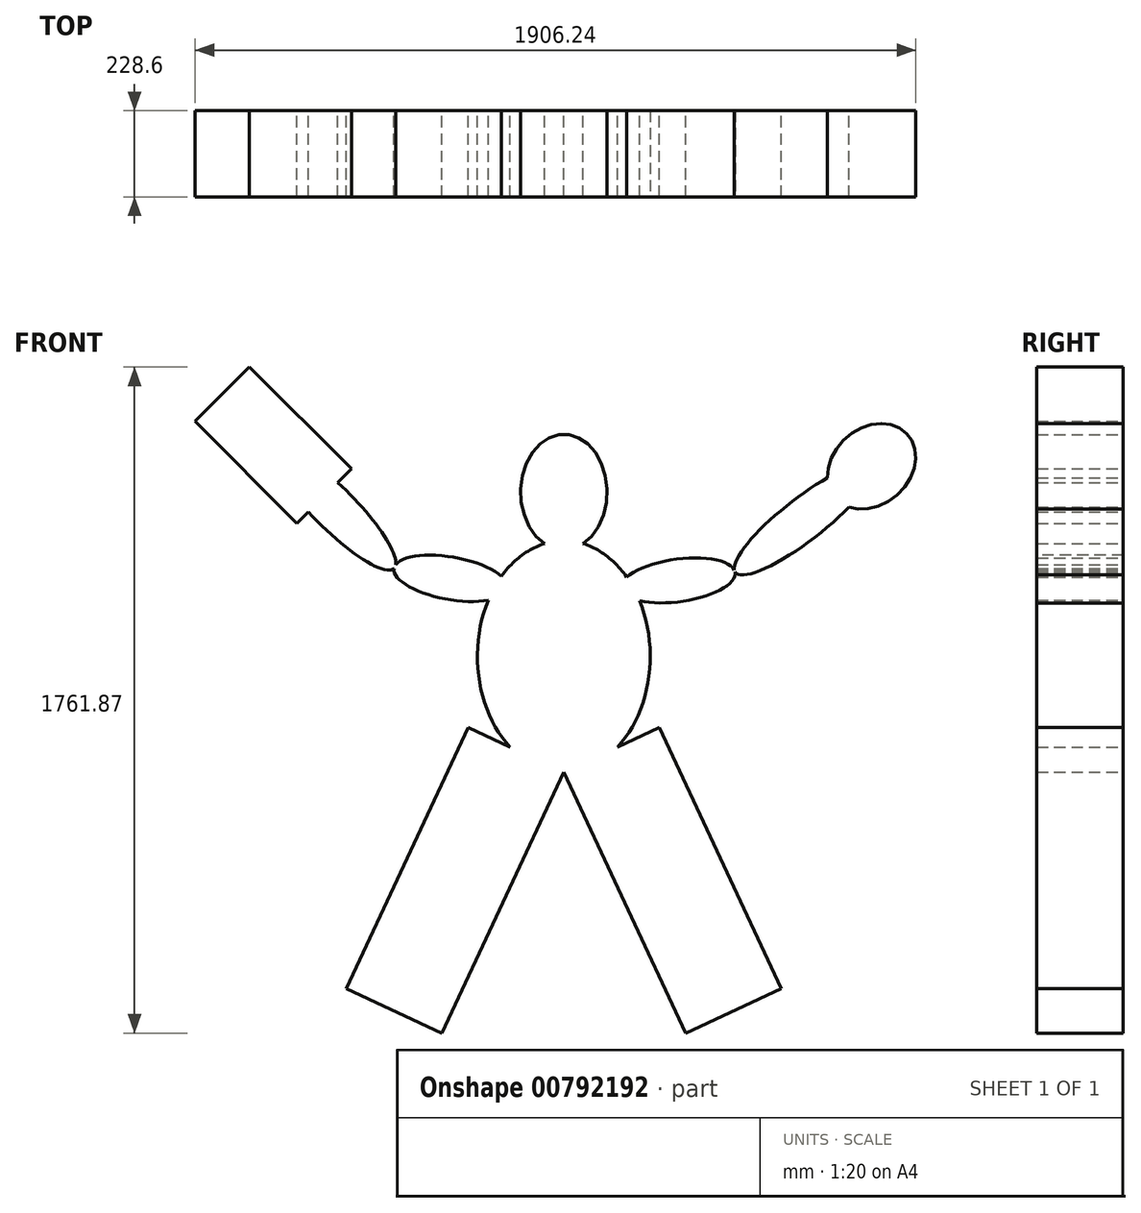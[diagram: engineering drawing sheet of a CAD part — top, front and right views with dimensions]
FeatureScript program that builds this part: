
annotation { "Feature Type Name" : "Feature", "Feature Type Description" : "" }
export const myFeature = defineFeature(function(context is Context, id is Id, definition is map)
    precondition{}
    {
        {
            var Q0;
            Q0=qCreatedBy(makeId("Front.planeOp"),FACE);
            var sketch = newSketch(context, id + "F0", { "sketchPlane" : qUnion([Q0])});
            skLineSegment(sketch, "E0.bottom", {"start": v(-670.73, 790.09) * mm, "end": v(-417.5, 908.17) * mm});
            skLineSegment(sketch, "E0.top", {"start": v(-348.7, 99.48) * mm, "end": v(-95.47, 217.56) * mm});
            skLineSegment(sketch, "E0.left", {"start": v(-670.73, 790.09) * mm, "end": v(-348.7, 99.48) * mm});
            skLineSegment(sketch, "E0.right", {"start": v(-417.5, 908.17) * mm, "end": v(-95.47, 217.56) * mm});
            skLineSegment(sketch, "E1", {"start": v(-670.73, 790.09) * mm, "end": v(-670.73, 666.94) * mm, "construction": true});
            skLineSegment(sketch, "E2.MirrorCS", {"start": v(-670.73, 790.09) * mm, "end": v(-992.76, 99.48) * mm});
            skLineSegment(sketch, "E3.MirrorCS", {"start": v(-670.73, 790.09) * mm, "end": v(-923.95, 908.17) * mm});
            skLineSegment(sketch, "E4.MirrorCS", {"start": v(-923.95, 908.17) * mm, "end": v(-1245.99, 217.56) * mm});
            skLineSegment(sketch, "E5.MirrorCS", {"start": v(-992.76, 99.48) * mm, "end": v(-1245.99, 217.56) * mm});
            skSolve(sketch);
        }
        {
            var Q0;
            Q0 = qSketchRegion(id + "F0", true);
            extrude(context, id + "F1", {"entities" : qUnion([Q0]), "depth" : 228.6 * mm, "offsetDistance" : 30.48 * mm});
        }
        {
            var Q0;
            Q0=qCreatedBy(makeId("Front.planeOp"),FACE);
            var sketch = newSketch(context, id + "F2", { "sketchPlane" : qUnion([Q0])});
            skPoint(sketch, "E6.0", {"position": v(-670.73, 790.09) * mm});
            skPoint(sketch, "E7.0", {"position": v(-417.5, 908.17) * mm});
            skPoint(sketch, "E8.orphan", {"position": v(-670.73, 0) * mm});
            skPoint(sketch, "E9", {"position": v(-670.73, 1402.08) * mm});
            skLineSegment(sketch, "E10", {"start": v(-670.73, 790.09) * mm, "end": v(-670.73, 0) * mm});
            skPoint(sketch, "E11", {"position": v(-670.73, 1706.88) * mm});
            skPoint(sketch, "E12.endSnap0", {"position": v(-670.73, 1096.08) * mm});
            skEllipse(sketch, "E13", {"center": v(-670.73, 1096.08) * mm, "majorRadius": 306 * mm, "minorRadius": 228.6 * mm, "majorAxis": v(0, -1)});
            skPoint(sketch, "E12.end.orphan", {"position": v(-442.13, 1096.08) * mm});
            skSolve(sketch);
        }
        {
            var Q0;
            Q0 = qSketchRegion(id + "F2", true);
            extrude(context, id + "F3", {"entities" : qUnion([Q0]), "operationType" : NewBodyOperationType.ADD, "depth" : 228.6 * mm, "offsetDistance" : 30.48 * mm});
        }
        {
            var Q0;
            Q0=qCreatedBy(makeId("Front.planeOp"),FACE);
            var sketch = newSketch(context, id + "F4", { "sketchPlane" : qUnion([Q0])});
            skPoint(sketch, "E14", {"position": v(-819.47, 1276.05) * mm});
            skPoint(sketch, "E15.0", {"position": v(-670.73, 790.09) * mm});
            skLineSegment(sketch, "E16", {"start": v(-670.73, 790.09) * mm, "end": v(-670.73, 1574.8) * mm});
            skPoint(sketch, "E17", {"position": v(-1439.3, 1654.8) * mm});
            skPoint(sketch, "E18", {"position": v(-722.55, 1300.13) * mm});
            skLineSegment(sketch, "E19", {"start": v(-819.47, 1276.05) * mm, "end": v(-868.54, 1459.2) * mm});
            skPoint(sketch, "E20", {"position": v(-1119.64, 1328.98) * mm});
            skEllipse(sketch, "E21", {"center": v(-969.55, 1302.52) * mm, "majorRadius": 152.4 * mm, "minorRadius": 56.25 * mm, "majorAxis": v(0.98, -0.17)});
            skEllipticalArc(sketch, "E22", {});
            skLineSegment(sketch, "E23", {"start": v(-1281.26, 1490.6) * mm, "end": v(-1119.64, 1328.98) * mm});
            skPoint(sketch, "E24", {"position": v(-1200.45, 1409.79) * mm});
            skLineSegment(sketch, "E25.bottom", {"start": v(-1502.16, 1861.35) * mm, "end": v(-1232.76, 1591.94) * mm});
            skLineSegment(sketch, "E25.top", {"start": v(-1645.85, 1717.66) * mm, "end": v(-1376.44, 1448.26) * mm});
            skLineSegment(sketch, "E25.left", {"start": v(-1502.16, 1861.35) * mm, "end": v(-1645.85, 1717.66) * mm});
            skLineSegment(sketch, "E25.right", {"start": v(-1232.76, 1591.94) * mm, "end": v(-1268.76, 1555.93) * mm});
            skPoint(sketch, "E25.middle", {"position": v(-1526, 1658.46) * mm});
            skEllipse(sketch, "E26.MirrorC", {"center": v(-368.72, 1296.96) * mm, "majorRadius": 152.4 * mm, "minorRadius": 56.25 * mm, "majorAxis": v(-1, -0.14)});
            skEllipticalArc(sketch, "E27.MirrorC", {});
            skEllipticalArc(sketch, "E28", {});
            skLineSegment(sketch, "E29.trimOffspring", {"start": v(-1346.6, 1478.1) * mm, "end": v(-1376.44, 1448.26) * mm});
            const initialGuessF4  = {"E22": [-1.2812554220077534, 1.4905974480104753, 0.707106781186547, -0.7071067811865482, 0.22856255143099563, 0.05578285008675462, 4.5481737622677105, 1.735011544911877], "E27.MirrorC": [-0.036755686022816036, 1.458448072047414, -0.7892457974895803, -0.6140774146189033, 0.22856255143099558, 0.055782850086754605, 4.169939510368037, 2.099765794468828], "E28": [0.14363634715759327, 1.59880317270886, -0.7549259145224532, -0.6558100819463192, 0.127, 0.1016, 0.42588074585773994, 5.72656272917314]};
            skSetInitialGuess(sketch, initialGuessF4);
            skSolve(sketch);
        }
        {
            var Q0;
            Q0 = qSketchRegion(id + "F4", true);
            extrude(context, id + "F5", {"entities" : qUnion([Q0]), "operationType" : NewBodyOperationType.ADD, "depth" : 228.6 * mm, "offsetDistance" : 30.48 * mm});
        }
        {
            var Q0;
            Q0=qCreatedBy(makeId("Front.planeOp"),FACE);
            var sketch = newSketch(context, id + "F6", { "sketchPlane" : qUnion([Q0])});
            skFitSpline(sketch, "E30.0", {"points": [v(-873.6, 1417.26) * mm, v(-867.73, 1429.43) * mm, v(-855.08, 1452.7) * mm, v(-833.63, 1484) * mm, v(-809.97, 1511.21) * mm, v(-784.45, 1534) * mm, v(-757.39, 1552.05) * mm, v(-729.16, 1565.12) * mm, v(-700.14, 1573.03) * mm, v(-670.73, 1575.68) * mm, v(-641.32, 1573.03) * mm, v(-612.3, 1565.12) * mm, v(-584.07, 1552.05) * mm, v(-557.01, 1534) * mm, v(-531.48, 1511.21) * mm, v(-507.83, 1484) * mm, v(-486.38, 1452.7) * mm, v(-473.73, 1429.43) * mm, v(-467.86, 1417.26) * mm], "construction": true});
            skLineSegment(sketch, "E31.bottom", {"start": v(-721.53, 1454.69) * mm, "end": v(-619.93, 1454.69) * mm, "construction": true});
            skLineSegment(sketch, "E31.top", {"start": v(-721.53, 1530.89) * mm, "end": v(-619.93, 1530.89) * mm, "construction": true});
            skLineSegment(sketch, "E31.left", {"start": v(-721.53, 1454.69) * mm, "end": v(-721.53, 1530.89) * mm, "construction": true});
            skLineSegment(sketch, "E31.right", {"start": v(-619.93, 1454.69) * mm, "end": v(-619.93, 1530.89) * mm, "construction": true});
            skEllipse(sketch, "E32", {"center": v(-670.73, 1530.89) * mm, "majorRadius": 152.4 * mm, "minorRadius": 114.3 * mm, "majorAxis": v(0, 1)});
            skSolve(sketch);
        }
        {
            var Q0;
            Q0 = qSketchRegion(id + "F6", true);
            extrude(context, id + "F7", {"entities" : qUnion([Q0]), "operationType" : NewBodyOperationType.ADD, "depth" : 228.6 * mm, "offsetDistance" : 30.48 * mm});
        }
    });
